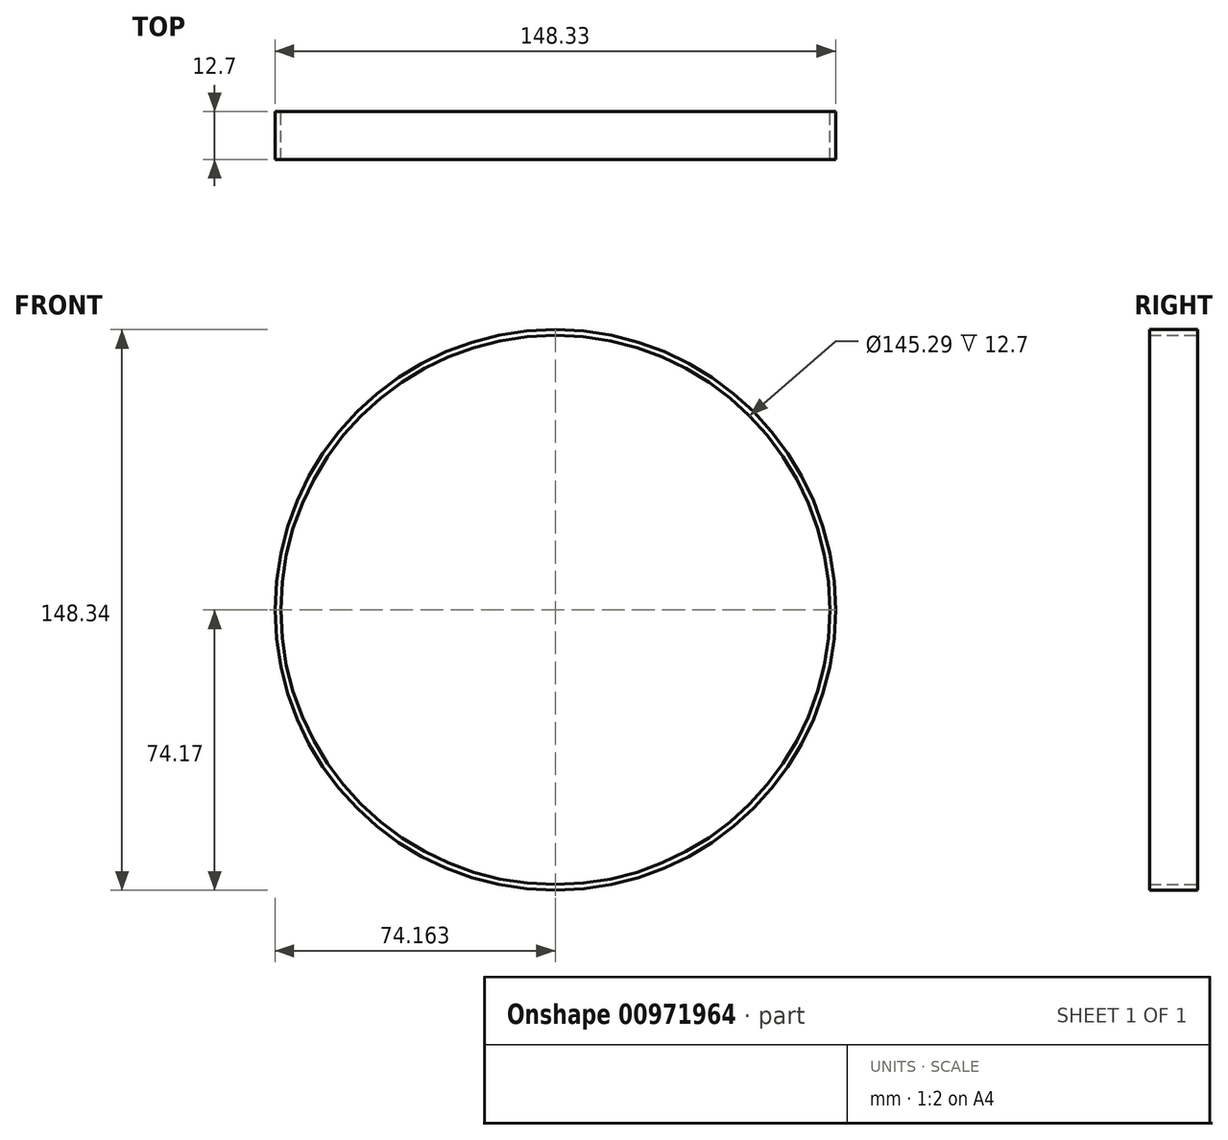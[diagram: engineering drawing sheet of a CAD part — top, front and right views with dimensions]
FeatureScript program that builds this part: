
annotation { "Feature Type Name" : "Feature", "Feature Type Description" : "" }
export const myFeature = defineFeature(function(context is Context, id is Id, definition is map)
    precondition{}
    {
        {
            var Q0;
            Q0=qCreatedBy(makeId("Top.planeOp"),FACE);
            var sketch = newSketch(context, id + "F0", { "sketchPlane" : qUnion([Q0])});
            skLineSegment(sketch, "E0.right", {"start": v(37.14, 57.5) * mm, "end": v(37.14, 51.14) * mm});
            skLineSegment(sketch, "E1", {"start": v(37.14, 51.14) * mm, "end": v(37.14, 44.8) * mm});
            skLineSegment(sketch, "E2", {"start": v(37.14, 51.14) * mm, "end": v(-37.03, 51.14) * mm});
            skLineSegment(sketch, "E3", {"start": v(-37.03, 51.14) * mm, "end": v(-37.03, 32.3) * mm});
            skLineSegment(sketch, "E4", {"start": v(37.14, 57.5) * mm, "end": v(35.62, 57.5) * mm});
            skLineSegment(sketch, "E5", {"start": v(35.62, 57.5) * mm, "end": v(35.62, 44.8) * mm});
            skLineSegment(sketch, "E6", {"start": v(35.62, 44.8) * mm, "end": v(37.14, 44.8) * mm});
            skSolve(sketch);
        }
        {
            var Q0;
            {var subQ0=sQuery(id+"F0.wireOp",EDGE,"E0.right");Q0=makeQuery(id+"F0.imprint","IMPRINT",FACE,{"disambiguationData":[TD([[makeQuery(id+"F0.imprint","IMPRINT",EDGE,{"derivedFrom":subQ0}),-1.0]])]});}
            var Q1;
            {var subQ0=sQuery(id+"F0.wireOp",EDGE,"E1");Q1=makeQuery(id+"F0.imprint","IMPRINT",FACE,{"disambiguationData":[TD([[makeQuery(id+"F0.imprint","IMPRINT",EDGE,{"derivedFrom":subQ0}),-1.0]])]});}
            var Q2;
            Q2=sQuery(id+"F0.wireOp",EDGE,"E3");
            revolve(context, id + "F1", {"surfaceOperationType" : NewSurfaceOperationType.NEW, "entities" : qUnion([Q0, Q1]), "axis" : qUnion([Q2]), "revolveType" : RevolveType.FULL});
        }
    });
